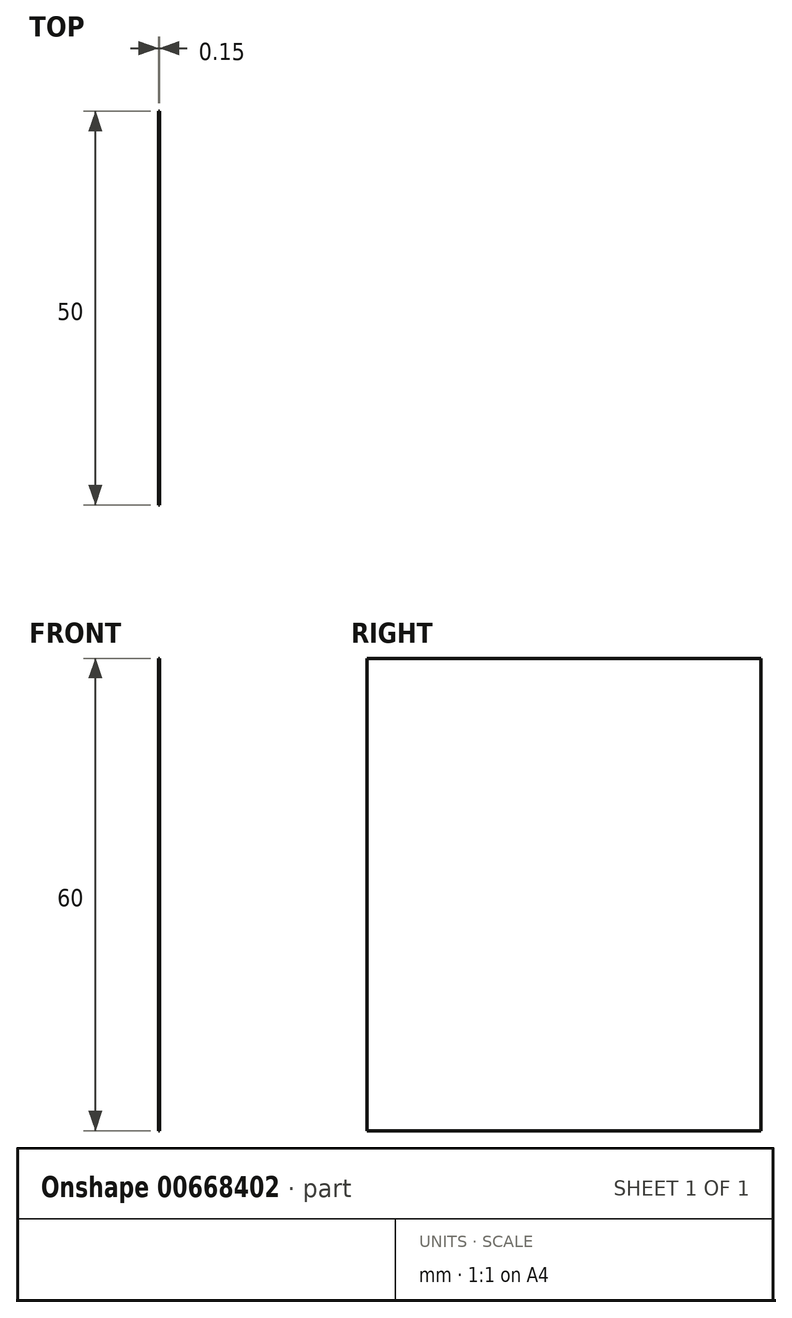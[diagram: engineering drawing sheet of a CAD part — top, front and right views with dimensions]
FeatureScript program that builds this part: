
annotation { "Feature Type Name" : "Feature", "Feature Type Description" : "" }
export const myFeature = defineFeature(function(context is Context, id is Id, definition is map)
    precondition{}
    {
        {
            var Q0;
            Q0=qCreatedBy(makeId("Right.planeOp"),FACE);
            var sketch = newSketch(context, id + "F0", { "sketchPlane" : qUnion([Q0])});
            skLineSegment(sketch, "E0.bottom", {"start": v(0, 0) * mm, "end": v(50, 0) * mm});
            skLineSegment(sketch, "E0.top", {"start": v(0, -60) * mm, "end": v(50, -60) * mm});
            skLineSegment(sketch, "E0.left", {"start": v(0, 0) * mm, "end": v(0, -60) * mm});
            skLineSegment(sketch, "E0.right", {"start": v(50, 0) * mm, "end": v(50, -60) * mm});
            skSolve(sketch);
        }
        {
            var Q0;
            Q0=makeQuery(id+"F0.imprint","IMPRINT",FACE,{"disambiguationData":[TD([[makeQuery(id+"F0.imprint","IMPRINT",EDGE,{"derivedFrom":sQuery(id+"F0.wireOp",EDGE,"E0.bottom")}),-1.0]])]});
            extrude(context, id + "F1", {"entities" : qUnion([Q0]), "depth" : .15 * mm, "offsetDistance" : 25 * mm});
        }
    });
